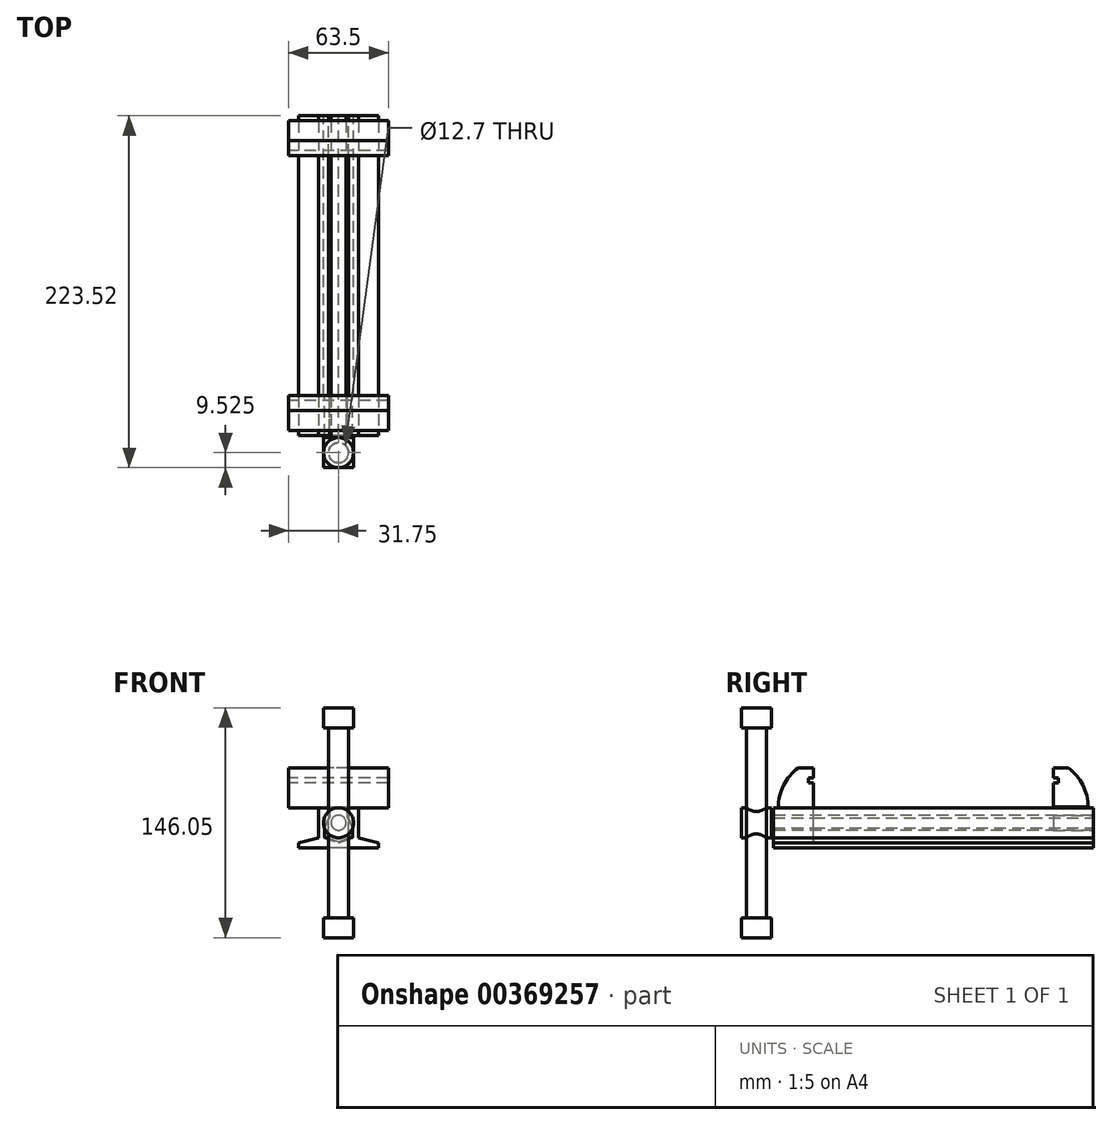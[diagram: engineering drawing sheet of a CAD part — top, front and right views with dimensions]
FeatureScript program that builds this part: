
annotation { "Feature Type Name" : "Feature", "Feature Type Description" : "" }
export const myFeature = defineFeature(function(context is Context, id is Id, definition is map)
    precondition{}
    {
        {
            var Q0;
            Q0=qCreatedBy(makeId("Front.planeOp"),FACE);
            var sketch = newSketch(context, id + "F0", { "sketchPlane" : qUnion([Q0])});
            skLineSegment(sketch, "E0.bottom", {"start": v(-12.7, 25.4) * mm, "end": v(12.7, 25.4) * mm});
            skLineSegment(sketch, "E0.top", {"start": v(-12.7, 0) * mm, "end": v(12.7, 0) * mm});
            skLineSegment(sketch, "E0.left", {"start": v(-12.7, 25.4) * mm, "end": v(-12.7, 6.35) * mm});
            skLineSegment(sketch, "E0.right", {"start": v(12.7, 25.4) * mm, "end": v(12.7, 6.35) * mm});
            skLineSegment(sketch, "E1", {"start": v(12.7, 6.35) * mm, "end": v(25.4, 3.17) * mm});
            skLineSegment(sketch, "E2", {"start": v(25.4, 3.17) * mm, "end": v(25.4, 0) * mm});
            skLineSegment(sketch, "E3", {"start": v(25.4, 0) * mm, "end": v(12.7, 0) * mm});
            skLineSegment(sketch, "E4", {"start": v(-12.7, 0) * mm, "end": v(-25.4, 0) * mm});
            skLineSegment(sketch, "E5", {"start": v(-25.4, 0) * mm, "end": v(-25.4, 3.17) * mm});
            skLineSegment(sketch, "E6", {"start": v(-25.4, 3.17) * mm, "end": v(-12.7, 6.35) * mm});
            skSolve(sketch);
        }
        {
            var Q0;
            Q0=makeQuery(id+"F0.imprint","IMPRINT",FACE,{"disambiguationData":[TD([[makeQuery(id+"F0.imprint","IMPRINT",EDGE,{"derivedFrom":sQuery(id+"F0.wireOp",EDGE,"E0.bottom")}),-1.0]])]});
            extrude(context, id + "F1", {"entities" : qUnion([Q0]), "endBound" : BoundingType.SYMMETRIC, "oppositeDirection" : true, "depth" : 203.2 * mm});
        }
        {
            var Q0;
            Q0=makeQuery(id+"F1.opExtrude","CAP_FACE",FACE,{"disambiguationData":[OSD([sQuery(id+"F0.wireOp",EDGE,"E0.bottom"),sQuery(id+"F0.wireOp",EDGE,"E0.top"),sQuery(id+"F0.wireOp",EDGE,"E0.left"),sQuery(id+"F0.wireOp",EDGE,"E0.right"),sQuery(id+"F0.wireOp",EDGE,"E1"),sQuery(id+"F0.wireOp",EDGE,"E2"),sQuery(id+"F0.wireOp",EDGE,"E3"),sQuery(id+"F0.wireOp",EDGE,"E4"),sQuery(id+"F0.wireOp",EDGE,"E5"),sQuery(id+"F0.wireOp",EDGE,"E6")])],"isStart":true});
            var sketch = newSketch(context, id + "F2", { "sketchPlane" : qUnion([Q0])});
            skCircle(sketch, "E7", {"center": v(0, 15.88) * mm, "radius": 4.76 * mm});
            skSolve(sketch);
        }
        {
            var Q0;
            Q0=makeQuery(id+"F2.imprint","IMPRINT",FACE,{"disambiguationData":[TD([[makeQuery(id+"F2.imprint","IMPRINT",EDGE,{"derivedFrom":sQuery(id+"F2.wireOp",EDGE,"E7")}),1.0]])]});
            var Q1;
            Q1=makeQuery(id+"F1.opExtrude","CAP_FACE",FACE,{"disambiguationData":[OSD([sQuery(id+"F0.wireOp",EDGE,"E0.bottom"),sQuery(id+"F0.wireOp",EDGE,"E0.top"),sQuery(id+"F0.wireOp",EDGE,"E0.left"),sQuery(id+"F0.wireOp",EDGE,"E0.right"),sQuery(id+"F0.wireOp",EDGE,"E1"),sQuery(id+"F0.wireOp",EDGE,"E2"),sQuery(id+"F0.wireOp",EDGE,"E3"),sQuery(id+"F0.wireOp",EDGE,"E4"),sQuery(id+"F0.wireOp",EDGE,"E5"),sQuery(id+"F0.wireOp",EDGE,"E6")])],"isStart":false});
            extrude(context, id + "F3", {"entities" : qUnion([Q0]), "operationType" : NewBodyOperationType.REMOVE, "endBound" : BoundingType.UP_TO_SURFACE, "oppositeDirection" : true, "endBoundEntityFace" : qUnion([Q1]), "depth" : 25.4 * mm});
        }
        {
            var Q0;
            Q0=makeQuery(id+"F1.opExtrude","CAP_FACE",FACE,{"disambiguationData":[OSD([sQuery(id+"F0.wireOp",EDGE,"E0.bottom"),sQuery(id+"F0.wireOp",EDGE,"E0.top"),sQuery(id+"F0.wireOp",EDGE,"E0.left"),sQuery(id+"F0.wireOp",EDGE,"E0.right"),sQuery(id+"F0.wireOp",EDGE,"E1"),sQuery(id+"F0.wireOp",EDGE,"E2"),sQuery(id+"F0.wireOp",EDGE,"E3"),sQuery(id+"F0.wireOp",EDGE,"E4"),sQuery(id+"F0.wireOp",EDGE,"E5"),sQuery(id+"F0.wireOp",EDGE,"E6")])],"isStart":false});
            var sketch = newSketch(context, id + "F4", { "sketchPlane" : qUnion([Q0])});
            skLineSegment(sketch, "E8", {"start": v(6.35, 25.4) * mm, "end": v(6.35, 19.05) * mm});
            skLineSegment(sketch, "E9", {"start": v(6.35, 19.05) * mm, "end": v(9.52, 12.7) * mm});
            skLineSegment(sketch, "E10", {"start": v(9.53, 12.7) * mm, "end": v(9.53, 6.35) * mm});
            skLineSegment(sketch, "E11", {"start": v(-9.53, 6.35) * mm, "end": v(-9.53, 12.7) * mm});
            skLineSegment(sketch, "E12", {"start": v(-9.52, 12.7) * mm, "end": v(-6.35, 19.05) * mm});
            skLineSegment(sketch, "E13", {"start": v(-6.35, 19.05) * mm, "end": v(-6.35, 25.4) * mm});
            skLineSegment(sketch, "E14", {"start": v(-6.35, 25.4) * mm, "end": v(6.35, 25.4) * mm});
            skLineSegment(sketch, "E15", {"start": v(9.53, 6.35) * mm, "end": v(0, 3.17) * mm});
            skLineSegment(sketch, "E16", {"start": v(0, 3.17) * mm, "end": v(-9.52, 6.35) * mm});
            skSolve(sketch);
        }
        {
            var Q0;
            Q0=makeQuery(id+"F4.imprint","IMPRINT",FACE,{"disambiguationData":[TD([[makeQuery(id+"F4.imprint","IMPRINT",EDGE,{"derivedFrom":sQuery(id+"F4.wireOp",EDGE,"E8")}),-1.0]])]});
            extrude(context, id + "F5", {"entities" : qUnion([Q0]), "operationType" : NewBodyOperationType.REMOVE, "oppositeDirection" : true, "depth" : 177.8 * mm});
        }
        {
            var Q0;
            Q0=qCreatedBy(makeId("Right.planeOp"),FACE);
            var sketch = newSketch(context, id + "F6", { "sketchPlane" : qUnion([Q0])});
            skPoint(sketch, "E17.0", {"position": v(-76.2, 25.4) * mm});
            skLineSegment(sketch, "E18", {"start": v(-76.2, 25.4) * mm, "end": v(-76.2, 41.27) * mm});
            skLineSegment(sketch, "E19", {"start": v(-76.2, 41.27) * mm, "end": v(-79.38, 41.27) * mm});
            skLineSegment(sketch, "E20", {"start": v(-79.38, 41.27) * mm, "end": v(-79.38, 44.45) * mm});
            skLineSegment(sketch, "E21", {"start": v(-79.38, 44.45) * mm, "end": v(-76.2, 44.45) * mm});
            skLineSegment(sketch, "E22", {"start": v(-76.2, 44.45) * mm, "end": v(-76.2, 50.8) * mm});
            skLineSegment(sketch, "E23", {"start": v(-76.2, 50.8) * mm, "end": v(-85.73, 50.8) * mm});
            skArc(sketch, "E24", {"start": v(-85.73, 50.8) * mm, "mid": v(-95.07, 39.6) * mm, "end": v(-98.43, 25.4) * mm});
            skLineSegment(sketch, "E25", {"start": v(-98.43, 25.4) * mm, "end": v(-76.2, 25.4) * mm});
            skSolve(sketch);
        }
        {
            var Q0;
            Q0=makeQuery(id+"F6.imprint","IMPRINT",FACE,{"disambiguationData":[TD([[makeQuery(id+"F6.imprint","IMPRINT",EDGE,{"derivedFrom":sQuery(id+"F6.wireOp",EDGE,"E18")}),1.0]])]});
            extrude(context, id + "F7", {"entities" : qUnion([Q0]), "operationType" : NewBodyOperationType.ADD, "endBound" : BoundingType.SYMMETRIC, "depth" : 63.5 * mm});
        }
        {
            var Q0;
            Q0=makeQuery(id+"F1.opExtrude","CAP_FACE",FACE,{"disambiguationData":[OSD([sQuery(id+"F0.wireOp",EDGE,"E0.bottom"),sQuery(id+"F0.wireOp",EDGE,"E0.top"),sQuery(id+"F0.wireOp",EDGE,"E0.left"),sQuery(id+"F0.wireOp",EDGE,"E0.right"),sQuery(id+"F0.wireOp",EDGE,"E1"),sQuery(id+"F0.wireOp",EDGE,"E2"),sQuery(id+"F0.wireOp",EDGE,"E3"),sQuery(id+"F0.wireOp",EDGE,"E4"),sQuery(id+"F0.wireOp",EDGE,"E5"),sQuery(id+"F0.wireOp",EDGE,"E6")])],"isStart":false});
            var sketch = newSketch(context, id + "F8", { "sketchPlane" : qUnion([Q0])});
            skLineSegment(sketch, "E26.0", {"start": v(-5.84, 18.93) * mm, "end": v(-5.84, 25.9) * mm});
            skLineSegment(sketch, "E26.1", {"start": v(-9.02, 12.58) * mm, "end": v(-5.84, 18.93) * mm});
            skLineSegment(sketch, "E26.2", {"start": v(-9.02, 6.72) * mm, "end": v(-9.02, 12.58) * mm});
            skLineSegment(sketch, "E26.3", {"start": v(0, 3.71) * mm, "end": v(-9.02, 6.72) * mm});
            skLineSegment(sketch, "E26.4", {"start": v(5.84, 25.9) * mm, "end": v(5.84, 18.93) * mm});
            skLineSegment(sketch, "E26.5", {"start": v(5.84, 18.93) * mm, "end": v(9.02, 12.58) * mm});
            skLineSegment(sketch, "E26.6", {"start": v(9.02, 12.58) * mm, "end": v(9.02, 6.72) * mm});
            skLineSegment(sketch, "E26.7", {"start": v(9.02, 6.72) * mm, "end": v(0, 3.71) * mm});
            skLineSegment(sketch, "E27", {"start": v(5.84, 25.9) * mm, "end": v(-5.84, 25.9) * mm});
            skSolve(sketch);
        }
        {
            var Q0;
            Q0=makeQuery(id+"F8.imprint","IMPRINT",FACE,{"disambiguationData":[TD([[makeQuery(id+"F8.imprint","IMPRINT",EDGE,{"derivedFrom":sQuery(id+"F8.wireOp",EDGE,"E26.0")}),-1.0]])]});
            extrude(context, id + "F9", {"entities" : qUnion([Q0]), "oppositeDirection" : true, "depth" : 25.4 * mm});
        }
        {
            var Q0;
            Q0=qCreatedBy(makeId("Right.planeOp"),FACE);
            var sketch = newSketch(context, id + "F10", { "sketchPlane" : qUnion([Q0])});
            skLineSegment(sketch, "E28.0", {"start": v(76.2, 25.9) * mm, "end": v(101.6, 25.9) * mm});
            skLineSegment(sketch, "E29", {"start": v(76.2, 41.27) * mm, "end": v(79.38, 41.27) * mm});
            skLineSegment(sketch, "E30", {"start": v(79.38, 41.27) * mm, "end": v(79.38, 44.45) * mm});
            skLineSegment(sketch, "E31", {"start": v(79.38, 44.45) * mm, "end": v(76.2, 44.45) * mm});
            skLineSegment(sketch, "E32", {"start": v(76.2, 44.45) * mm, "end": v(76.2, 50.8) * mm});
            skLineSegment(sketch, "E33", {"start": v(76.2, 50.8) * mm, "end": v(85.73, 50.8) * mm});
            skArc(sketch, "E34", {"start": v(98.43, 25.9) * mm, "mid": v(94.96, 39.83) * mm, "end": v(85.73, 50.8) * mm});
            skLineSegment(sketch, "E35", {"start": v(76.2, 25.9) * mm, "end": v(98.43, 25.9) * mm});
            skLineSegment(sketch, "E36", {"start": v(76.2, 41.27) * mm, "end": v(76.2, 25.9) * mm});
            skSolve(sketch);
        }
        {
            var Q0;
            Q0=makeQuery(id+"F10.imprint","IMPRINT",FACE,{"disambiguationData":[TD([[makeQuery(id+"F10.imprint","IMPRINT",EDGE,{"derivedFrom":sQuery(id+"F10.wireOp",EDGE,"E29")}),-1.0]])]});
            extrude(context, id + "F11", {"entities" : qUnion([Q0]), "operationType" : NewBodyOperationType.ADD, "endBound" : BoundingType.SYMMETRIC, "depth" : 63.5 * mm});
        }
        {
            var Q0;
            Q0=makeQuery(id+"F9.opExtrude","CAP_FACE",FACE,{"disambiguationData":[OSD([sQuery(id+"F8.wireOp",EDGE,"E26.0"),sQuery(id+"F8.wireOp",EDGE,"E26.1"),sQuery(id+"F8.wireOp",EDGE,"E26.2"),sQuery(id+"F8.wireOp",EDGE,"E26.3"),sQuery(id+"F8.wireOp",EDGE,"E26.4"),sQuery(id+"F8.wireOp",EDGE,"E26.5"),sQuery(id+"F8.wireOp",EDGE,"E26.6"),sQuery(id+"F8.wireOp",EDGE,"E26.7"),sQuery(id+"F8.wireOp",EDGE,"E27")])],"isStart":true});
            var sketch = newSketch(context, id + "F12", { "sketchPlane" : qUnion([Q0])});
            skCircle(sketch, "E37.0", {"center": v(0, 15.88) * mm, "radius": 4.76 * mm});
            skSolve(sketch);
        }
        {
            var Q0;
            Q0=makeQuery(id+"F12.imprint","IMPRINT",FACE,{"disambiguationData":[TD([[makeQuery(id+"F12.imprint","IMPRINT",EDGE,{"derivedFrom":sQuery(id+"F12.wireOp",EDGE,"E37.0")}),-1.0]])]});
            extrude(context, id + "F13", {"entities" : qUnion([Q0]), "operationType" : NewBodyOperationType.REMOVE, "endBound" : BoundingType.THROUGH_ALL, "oppositeDirection" : true, "depth" : 25.4 * mm});
        }
        {
            var Q0;
            Q0=makeQuery(id+"F2.imprint","IMPRINT",FACE,{"disambiguationData":[TD([[makeQuery(id+"F2.imprint","IMPRINT",EDGE,{"derivedFrom":sQuery(id+"F2.wireOp",EDGE,"E7")}),-1.0]])]});
            cPlane(context, id + "F14", {"entities" : qUnion([Q0]), "cplaneType" : CPlaneType.OFFSET, "offset" : 1.27 * mm, "width" : 152.4 * mm, "height" : 152.4 * mm});
        }
        {
            var Q0;
            Q0=qCreatedBy(id+"F14.planeOp",FACE);
            var sketch = newSketch(context, id + "F15", { "sketchPlane" : qUnion([Q0])});
            skCircle(sketch, "E38", {"center": v(0, 15.88) * mm, "radius": 4.76 * mm});
            skSolve(sketch);
        }
        {
            var Q0;
            Q0=makeQuery(id+"F15.imprint","IMPRINT",FACE,{"disambiguationData":[TD([[makeQuery(id+"F15.imprint","IMPRINT",EDGE,{"derivedFrom":sQuery(id+"F15.wireOp",EDGE,"E38")}),1.0]])]});
            var Q1;
            Q1=makeQuery(id+"F9.opExtrude","CAP_FACE",FACE,{"disambiguationData":[OSD([sQuery(id+"F8.wireOp",EDGE,"E26.0"),sQuery(id+"F8.wireOp",EDGE,"E26.1"),sQuery(id+"F8.wireOp",EDGE,"E26.2"),sQuery(id+"F8.wireOp",EDGE,"E26.3"),sQuery(id+"F8.wireOp",EDGE,"E26.4"),sQuery(id+"F8.wireOp",EDGE,"E26.5"),sQuery(id+"F8.wireOp",EDGE,"E26.6"),sQuery(id+"F8.wireOp",EDGE,"E26.7"),sQuery(id+"F8.wireOp",EDGE,"E27")])],"isStart":true});
            extrude(context, id + "F16", {"entities" : qUnion([Q0]), "endBound" : BoundingType.UP_TO_SURFACE, "oppositeDirection" : true, "endBoundEntityFace" : qUnion([Q1]), "depth" : 25.4 * mm});
        }
        {
            var Q0;
            Q0=qCreatedBy(id+"F14.planeOp",FACE);
            var sketch = newSketch(context, id + "F17", { "sketchPlane" : qUnion([Q0])});
            skCircle(sketch, "E39", {"center": v(0, 15.88) * mm, "radius": 9.53 * mm});
            skSolve(sketch);
        }
        {
            var Q0;
            Q0=makeQuery(id+"F17.imprint","IMPRINT",FACE,{"disambiguationData":[TD([[makeQuery(id+"F17.imprint","IMPRINT",EDGE,{"derivedFrom":sQuery(id+"F17.wireOp",EDGE,"E39")}),1.0]])]});
            extrude(context, id + "F18", {"entities" : qUnion([Q0]), "operationType" : NewBodyOperationType.ADD, "depth" : 19.05 * mm});
        }
        {
            var Q0;
            {var subQ0=sQuery(id+"F4.wireOp",EDGE,"E13");var subQ10=sQuery(id+"F0.wireOp",EDGE,"E0.bottom");Q0=makeQuery(id+"F7.boolean.opBoolean","SPLIT",FACE,{"disambiguationData":[TD([makeQuery(id+"F5.boolean.opBoolean","COPY",FACE,{"derivedFrom":makeQuery(id+"F5.opExtrude","SWEPT_FACE",FACE,{"disambiguationData":[OSD([subQ0])]})})])],"derivedFrom":makeQuery(id+"F1.opExtrude","SWEPT_FACE",FACE,{"disambiguationData":[OSD([subQ10])]})});}
            var sketch = newSketch(context, id + "F19", { "sketchPlane" : qUnion([Q0])});
            skCircle(sketch, "E40", {"center": v(0, -112.4) * mm, "radius": 6.35 * mm});
            skSolve(sketch);
        }
        {
            var Q0;
            Q0=makeQuery(id+"F19.imprint","IMPRINT",FACE,{"disambiguationData":[TD([[makeQuery(id+"F19.imprint","IMPRINT",EDGE,{"derivedFrom":sQuery(id+"F19.wireOp",EDGE,"E40")}),1.0]])]});
            extrude(context, id + "F20", {"entities" : qUnion([Q0]), "operationType" : NewBodyOperationType.REMOVE, "oppositeDirection" : true, "depth" : 25.4 * mm});
        }
        {
            var Q0;
            Q0=makeQuery(id+"F19.imprint","IMPRINT",FACE,{"disambiguationData":[TD([[makeQuery(id+"F19.imprint","IMPRINT",EDGE,{"derivedFrom":sQuery(id+"F19.wireOp",EDGE,"E40")}),1.0]])]});
            extrude(context, id + "F21", {"entities" : qUnion([Q0]), "depth" : 50.8 * mm, "hasSecondDirection" : true, "secondDirectionOppositeDirection" : true, "secondDirectionDepth" : 69.85 * mm});
        }
        {
            var Q0;
            Q0=makeQuery(id+"F21.opExtrude","CAP_FACE",FACE,{"disambiguationData":[OSD([sQuery(id+"F19.wireOp",EDGE,"E40")])],"isStart":false});
            var sketch = newSketch(context, id + "F22", { "sketchPlane" : qUnion([Q0])});
            skCircle(sketch, "E41", {"center": v(0, -112.4) * mm, "radius": 9.53 * mm});
            skSolve(sketch);
        }
        {
            var Q0;
            Q0=makeQuery(id+"F22.imprint","IMPRINT",FACE,{"disambiguationData":[TD([[makeQuery(id+"F22.imprint","IMPRINT",EDGE,{"derivedFrom":sQuery(id+"F22.wireOp",EDGE,"E41")}),1.0]])]});
            var Q1;
            Q1=makeQuery(id+"F22.imprint","IMPRINT",FACE,{"disambiguationData":[TD([[makeQuery(id+"F22.imprint","IMPRINT",EDGE,{"derivedFrom":makeQuery(id+"F21.opExtrude","CAP_EDGE",EDGE,{"disambiguationData":[OSD([sQuery(id+"F19.wireOp",EDGE,"E40")])],"isStart":false})}),1.0]])]});
            extrude(context, id + "F23", {"entities" : qUnion([Q0, Q1]), "operationType" : NewBodyOperationType.ADD, "depth" : 12.7 * mm});
        }
        {
            var Q0;
            Q0=makeQuery(id+"F21.opExtrude","CAP_FACE",FACE,{"disambiguationData":[OSD([sQuery(id+"F19.wireOp",EDGE,"E40")])],"isStart":true});
            var sketch = newSketch(context, id + "F24", { "sketchPlane" : qUnion([Q0])});
            skCircle(sketch, "E42.0", {"center": v(0, 112.4) * mm, "radius": 9.53 * mm});
            skSolve(sketch);
        }
        {
            var Q0;
            Q0=makeQuery(id+"F24.imprint","IMPRINT",FACE,{"disambiguationData":[TD([[makeQuery(id+"F24.imprint","IMPRINT",EDGE,{"derivedFrom":makeQuery(id+"F21.opExtrude","CAP_EDGE",EDGE,{"disambiguationData":[OSD([sQuery(id+"F19.wireOp",EDGE,"E40")])],"isStart":true})}),-1.0]])]});
            var Q1;
            Q1=makeQuery(id+"F24.imprint","IMPRINT",FACE,{"disambiguationData":[TD([[makeQuery(id+"F24.imprint","IMPRINT",EDGE,{"derivedFrom":sQuery(id+"F24.wireOp",EDGE,"E42.0")}),1.0]])]});
            extrude(context, id + "F25", {"entities" : qUnion([Q0, Q1]), "operationType" : NewBodyOperationType.ADD, "depth" : 12.7 * mm});
        }
    });
